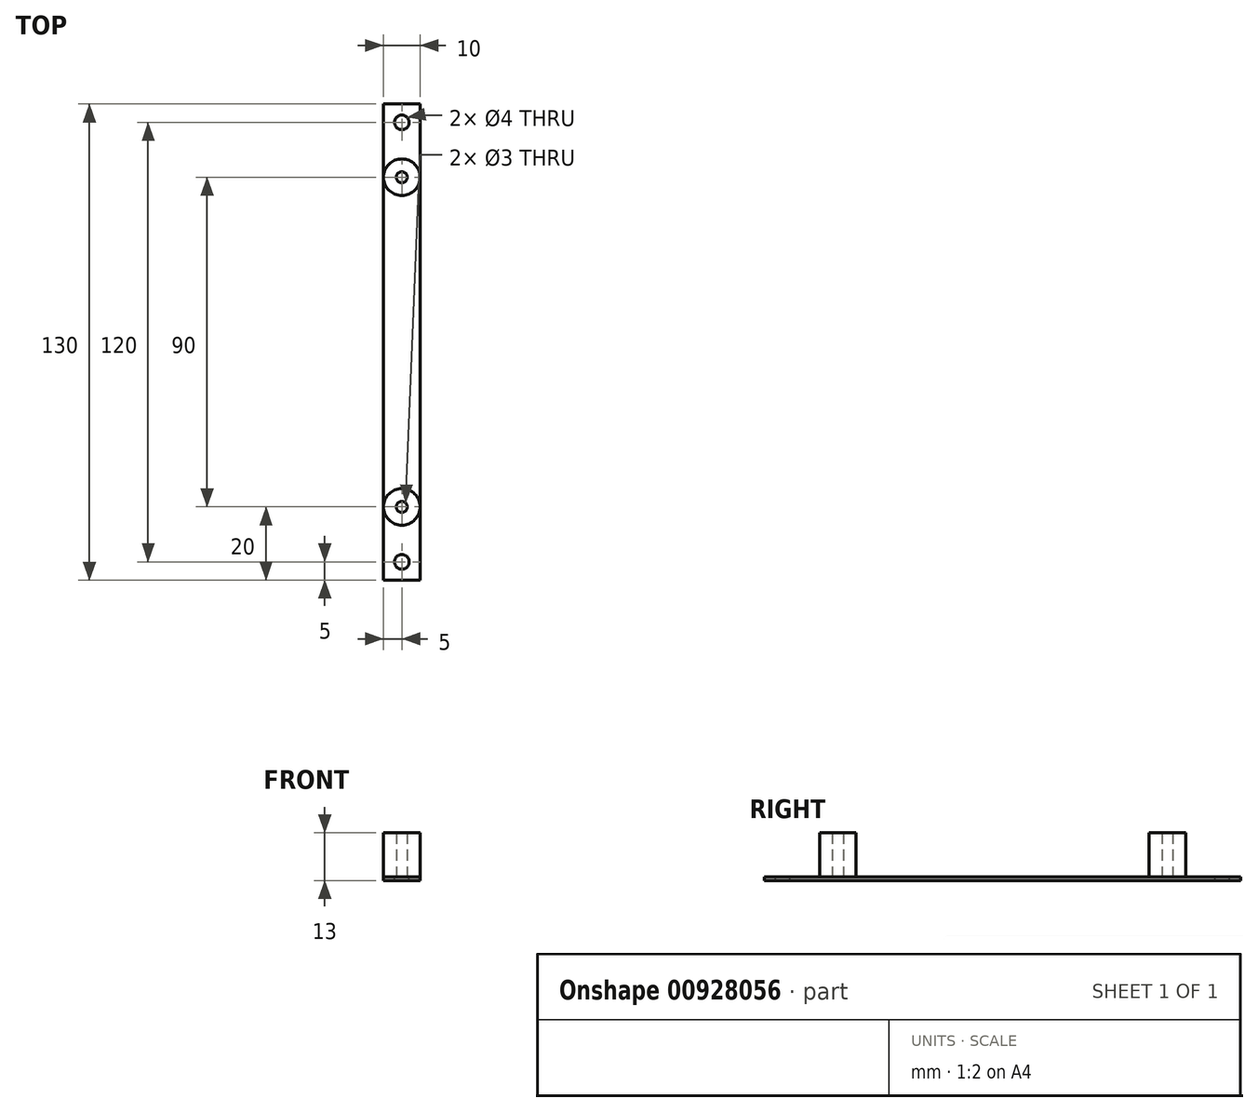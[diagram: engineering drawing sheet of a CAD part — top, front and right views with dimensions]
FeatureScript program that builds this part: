
annotation { "Feature Type Name" : "Feature", "Feature Type Description" : "" }
export const myFeature = defineFeature(function(context is Context, id is Id, definition is map)
    precondition{}
    {
        {
            var Q0;
            Q0=qCreatedBy(makeId("Top.planeOp"),FACE);
            var sketch = newSketch(context, id + "F0", { "sketchPlane" : qUnion([Q0])});
            skLineSegment(sketch, "E0.bottom", {"start": v(5, -65) * mm, "end": v(-5, -65) * mm});
            skLineSegment(sketch, "E0.top", {"start": v(5, 65) * mm, "end": v(-5, 65) * mm});
            skLineSegment(sketch, "E0.left", {"start": v(5, -65) * mm, "end": v(5, 65) * mm});
            skLineSegment(sketch, "E0.right", {"start": v(-5, -65) * mm, "end": v(-5, 65) * mm});
            skPoint(sketch, "E0.middle", {"position": v(0, 0) * mm});
            skSolve(sketch);
        }
        {
            var Q0;
            Q0=makeQuery(id+"F0.imprint","IMPRINT",FACE,{"disambiguationData":[TD([[makeQuery(id+"F0.imprint","IMPRINT",EDGE,{"derivedFrom":sQuery(id+"F0.wireOp",EDGE,"E0.bottom")}),-1.0]])]});
            extrude(context, id + "F1", {"entities" : qUnion([Q0]), "depth" : 1 * mm, "offsetDistance" : 25 * mm});
        }
        {
            var Q0;
            Q0=makeQuery(id+"F1.opExtrude","CAP_FACE",FACE,{"disambiguationData":[OSD([sQuery(id+"F0.wireOp",EDGE,"E0.bottom"),sQuery(id+"F0.wireOp",EDGE,"E0.top"),sQuery(id+"F0.wireOp",EDGE,"E0.left"),sQuery(id+"F0.wireOp",EDGE,"E0.right")])],"isStart":false});
            var sketch = newSketch(context, id + "F2", { "sketchPlane" : qUnion([Q0])});
            skCircle(sketch, "E1", {"center": v(0, 60) * mm, "radius": 2 * mm});
            skCircle(sketch, "E2.1.0", {"center": v(0, -60) * mm, "radius": 2 * mm});
            skPoint(sketch, "E2.center", {"position": v(0, 0) * mm});
            skSolve(sketch);
        }
        {
            var Q0;
            Q0=makeQuery(id+"F2.imprint","IMPRINT",FACE,{"disambiguationData":[TD([[makeQuery(id+"F2.imprint","IMPRINT",EDGE,{"derivedFrom":sQuery(id+"F2.wireOp",EDGE,"E1")}),1.0]])]});
            var Q1;
            Q1=makeQuery(id+"F2.imprint","IMPRINT",FACE,{"disambiguationData":[TD([[makeQuery(id+"F2.imprint","IMPRINT",EDGE,{"derivedFrom":sQuery(id+"F2.wireOp",EDGE,"E2.1.0")}),1.0]])]});
            extrude(context, id + "F3", {"entities" : qUnion([Q0, Q1]), "operationType" : NewBodyOperationType.REMOVE, "oppositeDirection" : true, "depth" : 25 * mm, "offsetDistance" : 25 * mm});
        }
        {
            var Q0;
            Q0=makeQuery(id+"F1.opExtrude","CAP_FACE",FACE,{"disambiguationData":[OSD([sQuery(id+"F0.wireOp",EDGE,"E0.bottom"),sQuery(id+"F0.wireOp",EDGE,"E0.top"),sQuery(id+"F0.wireOp",EDGE,"E0.left"),sQuery(id+"F0.wireOp",EDGE,"E0.right")])],"isStart":false});
            var sketch = newSketch(context, id + "F4", { "sketchPlane" : qUnion([Q0])});
            skCircle(sketch, "E3", {"center": v(0, 45) * mm, "radius": 5 * mm});
            skCircle(sketch, "E4.1.0", {"center": v(0, -45) * mm, "radius": 5 * mm});
            skPoint(sketch, "E4.center", {"position": v(0, 0) * mm});
            skSolve(sketch);
        }
        {
            var Q0;
            {var subQ0=sQuery(id+"F4.wireOp",EDGE,"E3");var subQ1=makeQuery(id+"F4.imprint","INTERSECT",VERTEX,{"derivedFrom":[makeQuery(id+"F1.opExtrude","CAP_EDGE",EDGE,{"disambiguationData":[OSD([sQuery(id+"F0.wireOp",EDGE,"E0.left")])],"isStart":false}),subQ0]});Q0=makeQuery(id+"F4.imprint","IMPRINT",FACE,{"disambiguationData":[TD([[makeQuery(id+"F4.imprint","IMPRINT",EDGE,{"disambiguationData":[TD([[subQ1,-1.0]])],"derivedFrom":subQ0}),1.0]])]});}
            var Q1;
            {var subQ0=sQuery(id+"F4.wireOp",EDGE,"E4.1.0");var subQ1=makeQuery(id+"F4.imprint","INTERSECT",VERTEX,{"derivedFrom":[makeQuery(id+"F1.opExtrude","CAP_EDGE",EDGE,{"disambiguationData":[OSD([sQuery(id+"F0.wireOp",EDGE,"E0.left")])],"isStart":false}),subQ0]});Q1=makeQuery(id+"F4.imprint","IMPRINT",FACE,{"disambiguationData":[TD([[makeQuery(id+"F4.imprint","IMPRINT",EDGE,{"disambiguationData":[TD([[subQ1,1.0]])],"derivedFrom":subQ0}),1.0]])]});}
            extrude(context, id + "F5", {"entities" : qUnion([Q0, Q1]), "operationType" : NewBodyOperationType.ADD, "depth" : 12 * mm, "offsetDistance" : 25 * mm});
        }
        {
            var Q0;
            Q0=makeQuery(id+"F1.opExtrude","CAP_FACE",FACE,{"disambiguationData":[OSD([sQuery(id+"F0.wireOp",EDGE,"E0.bottom"),sQuery(id+"F0.wireOp",EDGE,"E0.top"),sQuery(id+"F0.wireOp",EDGE,"E0.left"),sQuery(id+"F0.wireOp",EDGE,"E0.right")])],"isStart":true});
            var sketch = newSketch(context, id + "F6", { "sketchPlane" : qUnion([Q0])});
            skCircle(sketch, "E5", {"center": v(0, -45) * mm, "radius": 1.5 * mm});
            skCircle(sketch, "E6.1.0", {"center": v(0, 45) * mm, "radius": 1.5 * mm});
            skPoint(sketch, "E6.center", {"position": v(0, 0) * mm});
            skSolve(sketch);
        }
        {
            var Q0;
            Q0=makeQuery(id+"F6.imprint","IMPRINT",FACE,{"disambiguationData":[TD([[makeQuery(id+"F6.imprint","IMPRINT",EDGE,{"derivedFrom":sQuery(id+"F6.wireOp",EDGE,"E5")}),1.0]])]});
            var Q1;
            Q1=makeQuery(id+"F6.imprint","IMPRINT",FACE,{"disambiguationData":[TD([[makeQuery(id+"F6.imprint","IMPRINT",EDGE,{"derivedFrom":sQuery(id+"F6.wireOp",EDGE,"E6.1.0")}),1.0]])]});
            extrude(context, id + "F7", {"entities" : qUnion([Q0, Q1]), "operationType" : NewBodyOperationType.REMOVE, "oppositeDirection" : true, "depth" : 25 * mm, "offsetDistance" : 25 * mm});
        }
    });
